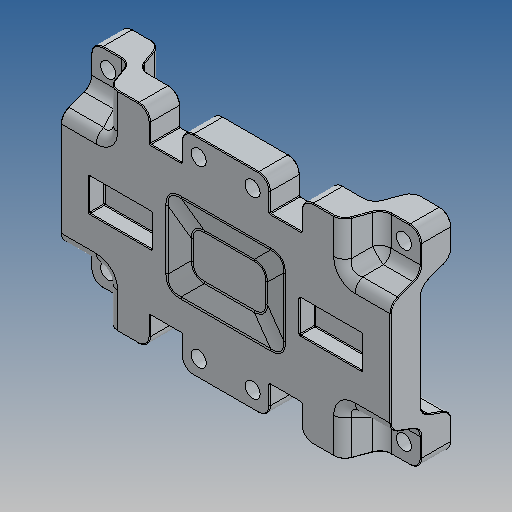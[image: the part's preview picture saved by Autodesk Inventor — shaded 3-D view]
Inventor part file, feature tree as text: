
AUTODESK INVENTOR PART (.ipt)
format: ipt  version: 2025 (Build 290162010, 162A)  size: 1,084,416 bytes
history: native  units: mm
features: extrude x8, sketch x8, fillet x3, mirror x3, other x2
ambient origin geometry x8: Origin, YZ Plane, XZ Plane, XY Plane, X Axis, Y Axis, Z Axis, Center Point
bodies: Volumenkörper1 (feature_tree)
feature tree (24):
  extrude  "Extrusion1"  Depth=43.5mm
  extrude  "Extrusion2"  Depth=12.911762mm
  other  "Flächenverjüngung1"
  extrude  "Extrusion3"  Depth=3.490659mm
  extrude  "Extrusion4"  Depth=8.0mm
  extrude  "Extrusion5"  Depth=10.0mm
  extrude  "Extrusion6"  Depth=19.5mm
  other  "Flächenverjüngung2"
  fillet  "Rundung1"  Radius=8.4mm
  mirror  "Spiegeln1"
  extrude  "Extrusion7"  TaperAngle=0.0deg  [1 undecoded]
  fillet  "Rundung2"  Radius=16.5mm
  fillet  "Rundung3"  Radius=4.25mm
  mirror  "Spiegeln2"
  mirror  "Spiegeln3"
  extrude  "Extrusion8"  Depth=4.0mm TaperAngle=0.0deg
  sketch  "Skizze1"  dims[d0=27.5mm d1=43.5mm]
  sketch  "Skizze2"  dims[d2=8.0mm d3=0.0mm d4=12.911762mm]
  sketch  "Skizze3"  dims[d5=8.0mm d6=0.0mm d9=3.490659mm]
  sketch  "Skizze4"  dims[d10=3.490659mm d11=8.0mm]
  sketch  "Skizze5"  dims[d12=10.0mm d13=10.0mm]
  sketch  "Skizze6"  dims[d14=8.0mm d15=3.490659mm d16=19.5mm d17=8.4mm]
  sketch  "Skizze7"  dims[d18=20.0mm d19=0.0mm d20=0.0mm d21=16.5mm d22=4.25mm]
  sketch  "Skizze8"  dims[d23=36.0mm d24=4.0mm d25=0.0mm d26=4.0mm d29=9.828718mm d30=5.828718mm d31=1.0mm d32=0.0mm d33=13.962634mm d34=11.5mm d35=15.5mm d36=1.745329mm d37=1.0mm d38=7.547497mm d39=5.671282mm d40=20.0mm d41=4.0mm d42=4.5mm d43=4.5mm d44=4.0mm d45=0.0mm d46=4.5mm d47=4.5mm d48=3.0mm d49=0.2mm d50=0.2mm d51=1.5mm d52=5.0mm d53=0.1mm d54=0.0mm]
note: 1 required parameter value undecoded (feature->parameter linkage not recoverable at this tier; creation-order binding heuristic only, values carry confidence <= 0.55)
